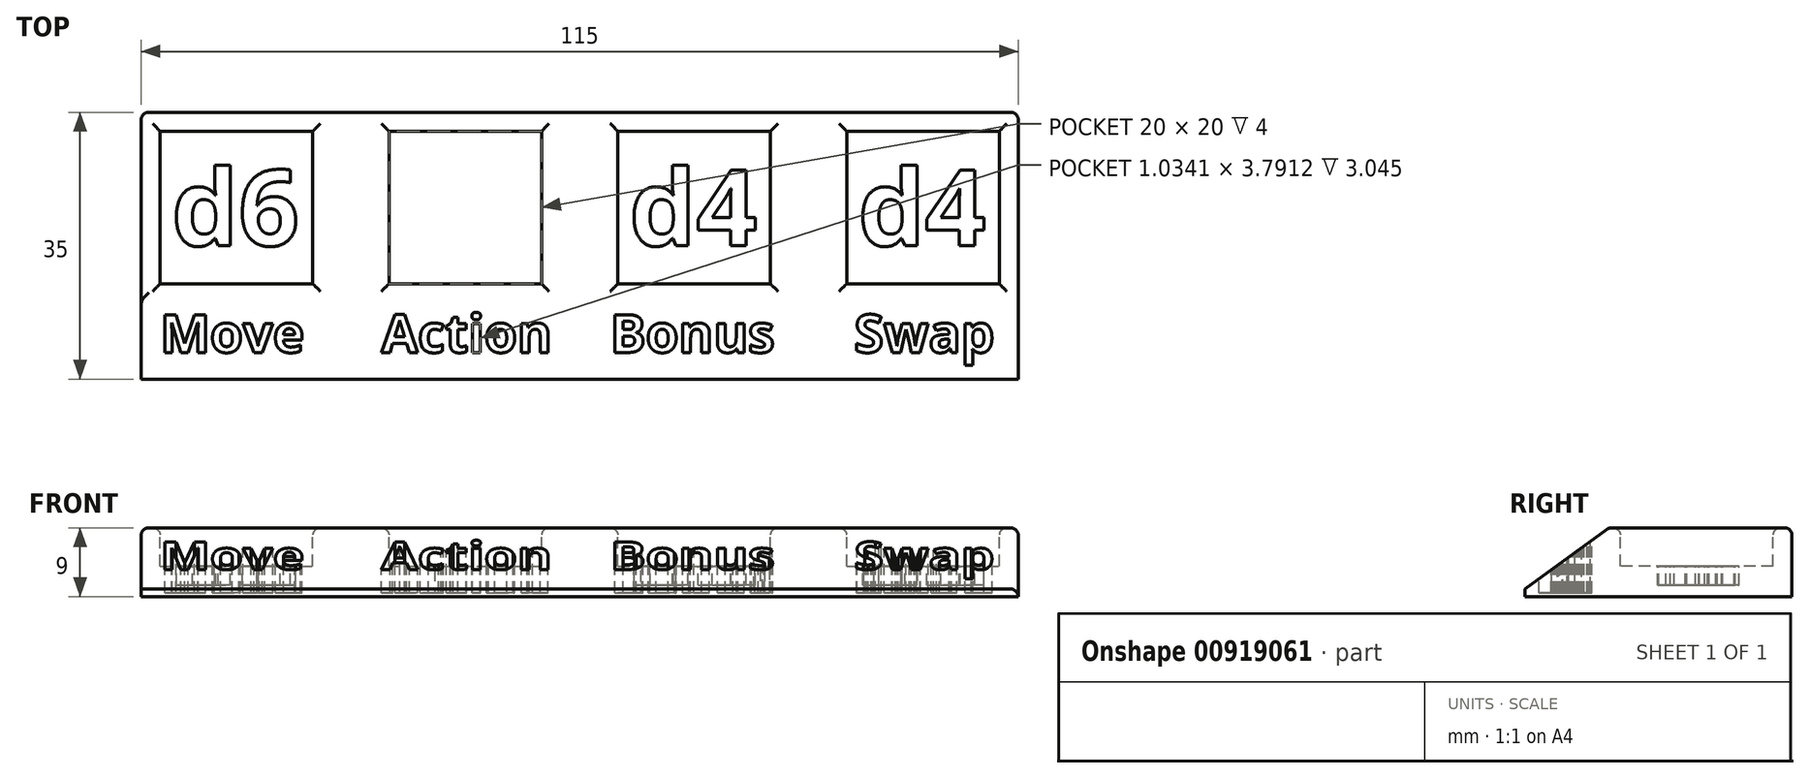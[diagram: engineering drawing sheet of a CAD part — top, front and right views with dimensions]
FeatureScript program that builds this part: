
annotation { "Feature Type Name" : "Feature", "Feature Type Description" : "" }
export const myFeature = defineFeature(function(context is Context, id is Id, definition is map)
    precondition{}
    {
        {
            var Q0;
            Q0=qCreatedBy(makeId("Top.planeOp"),FACE);
            var sketch = newSketch(context, id + "F0", { "sketchPlane" : qUnion([Q0])});
            skLineSegment(sketch, "E0.bottom", {"start": v(0, 0) * mm, "end": v(115, 0) * mm});
            skLineSegment(sketch, "E0.top", {"start": v(0, 35) * mm, "end": v(115, 35) * mm});
            skLineSegment(sketch, "E0.left", {"start": v(0, 0) * mm, "end": v(0, 35) * mm});
            skLineSegment(sketch, "E0.right", {"start": v(115, 0) * mm, "end": v(115, 35) * mm});
            skLineSegment(sketch, "E1", {"start": v(0, 32.5) * mm, "end": v(115, 32.5) * mm, "construction": true});
            skLineSegment(sketch, "E2", {"start": v(0, 12.5) * mm, "end": v(115, 12.5) * mm, "construction": true});
            skLineSegment(sketch, "E3.bottom", {"start": v(2.5, 32.5) * mm, "end": v(22.5, 32.5) * mm});
            skLineSegment(sketch, "E3.top", {"start": v(2.5, 12.5) * mm, "end": v(22.5, 12.5) * mm});
            skLineSegment(sketch, "E3.left", {"start": v(2.5, 32.5) * mm, "end": v(2.5, 12.5) * mm});
            skLineSegment(sketch, "E3.right", {"start": v(22.5, 32.5) * mm, "end": v(22.5, 12.5) * mm});
            skLineSegment(sketch, "E4.bottom", {"start": v(32.5, 32.5) * mm, "end": v(52.5, 32.5) * mm});
            skLineSegment(sketch, "E4.top", {"start": v(32.5, 12.5) * mm, "end": v(52.5, 12.5) * mm});
            skLineSegment(sketch, "E4.left", {"start": v(32.5, 32.5) * mm, "end": v(32.5, 12.5) * mm});
            skLineSegment(sketch, "E4.right", {"start": v(52.5, 32.5) * mm, "end": v(52.5, 12.5) * mm});
            skLineSegment(sketch, "E5.bottom", {"start": v(62.5, 32.5) * mm, "end": v(82.5, 32.5) * mm});
            skLineSegment(sketch, "E5.top", {"start": v(62.5, 12.5) * mm, "end": v(82.5, 12.5) * mm});
            skLineSegment(sketch, "E5.left", {"start": v(62.5, 32.5) * mm, "end": v(62.5, 12.5) * mm});
            skLineSegment(sketch, "E5.right", {"start": v(82.5, 32.5) * mm, "end": v(82.5, 12.5) * mm});
            skLineSegment(sketch, "E6.bottom", {"start": v(92.5, 32.5) * mm, "end": v(112.5, 32.5) * mm});
            skLineSegment(sketch, "E6.top", {"start": v(92.5, 12.5) * mm, "end": v(112.5, 12.5) * mm});
            skLineSegment(sketch, "E6.left", {"start": v(92.5, 32.5) * mm, "end": v(92.5, 12.5) * mm});
            skLineSegment(sketch, "E6.right", {"start": v(112.5, 32.5) * mm, "end": v(112.5, 12.5) * mm});
            skLineSegment(sketch, "E7", {"start": v(0, 27.5) * mm, "end": v(115, 27.5) * mm, "construction": true});
            skLineSegment(sketch, "E8", {"start": v(0, 17.5) * mm, "end": v(115, 17.5) * mm, "construction": true});
            skText(sketch, "E9", { "text": "d6", "fontName": "OpenSans-Bold.ttf"});
            skText(sketch, "E10", { "text": "d4", "fontName": "OpenSans-Bold.ttf"});
            skText(sketch, "E11", { "text": "d4", "fontName": "OpenSans-Bold.ttf"});
            skLineSegment(sketch, "E12", {"start": v(0, 3.5) * mm, "end": v(115, 3.5) * mm, "construction": true});
            skLineSegment(sketch, "E13", {"start": v(0, 8.5) * mm, "end": v(115, 8.5) * mm, "construction": true});
            skText(sketch, "E14", { "text": "Move", "fontName": "OpenSans-Bold.ttf"});
            skText(sketch, "E15", { "text": "Action", "fontName": "OpenSans-Bold.ttf"});
            skText(sketch, "E16", { "text": "Bonus", "fontName": "OpenSans-Bold.ttf"});
            skText(sketch, "E17", { "text": "Swap", "fontName": "OpenSans-Bold.ttf"});
            const initialGuessF0  = {"E9": [0.004, 0.0175, 1, 0, 0.01], "E10": [0.064, 0.0175, 1, 0, 0.01], "E11": [0.094, 0.0175, 1, 0, 0.01], "E14": [0.0025, 0.0035, 1, 0, 0.005], "E15": [0.0315, 0.0035, 1, 0, 0.005], "E16": [0.0615, 0.0035, 1, 0, 0.005], "E17": [0.0935, 0.0035, 1, 0, 0.005]};
            skSetInitialGuess(sketch, initialGuessF0);
            skSolve(sketch);
        }
        {
            var Q0;
            Q0=makeQuery(id+"F0.imprint","IMPRINT",FACE,{"disambiguationData":[TD([[makeQuery(id+"F0.imprint","IMPRINT",EDGE,{"derivedFrom":sQuery(id+"F0.wireOp",EDGE,"E0.bottom")}),1.0]])]});
            var Q1;
            Q1=makeQuery(id+"F0.imprint","IMPRINT",FACE,{"disambiguationData":[TD([[makeQuery(id+"F0.imprint","IMPRINT",EDGE,{"derivedFrom":sQuery(id+"F0.wireOp",EDGE,"E11.sketch_text.stroke-0")}),-1.0]])]});
            var Q2;
            Q2=makeQuery(id+"F0.imprint","IMPRINT",FACE,{"disambiguationData":[TD([[makeQuery(id+"F0.imprint","IMPRINT",EDGE,{"derivedFrom":sQuery(id+"F0.wireOp",EDGE,"E17.sketch_text.stroke-54")}),-1.0]])]});
            var Q3;
            Q3=makeQuery(id+"F0.imprint","IMPRINT",FACE,{"disambiguationData":[TD([[makeQuery(id+"F0.imprint","IMPRINT",EDGE,{"derivedFrom":sQuery(id+"F0.wireOp",EDGE,"E16.sketch_text.stroke-60")}),-1.0]])]});
            var Q4;
            Q4=makeQuery(id+"F0.imprint","IMPRINT",FACE,{"disambiguationData":[TD([[makeQuery(id+"F0.imprint","IMPRINT",EDGE,{"derivedFrom":sQuery(id+"F0.wireOp",EDGE,"E5.bottom")}),-1.0]])]});
            var Q5;
            Q5=makeQuery(id+"F0.imprint","IMPRINT",FACE,{"disambiguationData":[TD([[makeQuery(id+"F0.imprint","IMPRINT",EDGE,{"derivedFrom":sQuery(id+"F0.wireOp",EDGE,"E4.bottom")}),-1.0]])]});
            var Q6;
            Q6=makeQuery(id+"F0.imprint","IMPRINT",FACE,{"disambiguationData":[TD([[makeQuery(id+"F0.imprint","IMPRINT",EDGE,{"derivedFrom":sQuery(id+"F0.wireOp",EDGE,"E15.sketch_text.stroke-53")}),1.0]])]});
            var Q7;
            Q7=makeQuery(id+"F0.imprint","IMPRINT",FACE,{"disambiguationData":[TD([[makeQuery(id+"F0.imprint","IMPRINT",EDGE,{"derivedFrom":sQuery(id+"F0.wireOp",EDGE,"E16.sketch_text.stroke-19")}),1.0]])]});
            var Q8;
            Q8=makeQuery(id+"F0.imprint","IMPRINT",FACE,{"disambiguationData":[TD([[makeQuery(id+"F0.imprint","IMPRINT",EDGE,{"derivedFrom":sQuery(id+"F0.wireOp",EDGE,"E17.sketch_text.stroke-0")}),-1.0]])]});
            var Q9;
            Q9=makeQuery(id+"F0.imprint","IMPRINT",FACE,{"disambiguationData":[TD([[makeQuery(id+"F0.imprint","IMPRINT",EDGE,{"derivedFrom":sQuery(id+"F0.wireOp",EDGE,"E15.sketch_text.stroke-49")}),-1.0]])]});
            var Q10;
            Q10=makeQuery(id+"F0.imprint","IMPRINT",FACE,{"disambiguationData":[TD([[makeQuery(id+"F0.imprint","IMPRINT",EDGE,{"derivedFrom":sQuery(id+"F0.wireOp",EDGE,"E14.sketch_text.stroke-37")}),-1.0]])]});
            var Q11;
            Q11=makeQuery(id+"F0.imprint","IMPRINT",FACE,{"disambiguationData":[TD([[makeQuery(id+"F0.imprint","IMPRINT",EDGE,{"derivedFrom":sQuery(id+"F0.wireOp",EDGE,"E15.sketch_text.stroke-8")}),1.0]])]});
            var Q12;
            Q12=makeQuery(id+"F0.imprint","IMPRINT",FACE,{"disambiguationData":[TD([[makeQuery(id+"F0.imprint","IMPRINT",EDGE,{"derivedFrom":sQuery(id+"F0.wireOp",EDGE,"E10.sketch_text.stroke-14")}),1.0]])]});
            var Q13;
            Q13=makeQuery(id+"F0.imprint","IMPRINT",FACE,{"disambiguationData":[TD([[makeQuery(id+"F0.imprint","IMPRINT",EDGE,{"derivedFrom":sQuery(id+"F0.wireOp",EDGE,"E9.sketch_text.stroke-0")}),-1.0]])]});
            var Q14;
            Q14=makeQuery(id+"F0.imprint","IMPRINT",FACE,{"disambiguationData":[TD([[makeQuery(id+"F0.imprint","IMPRINT",EDGE,{"derivedFrom":sQuery(id+"F0.wireOp",EDGE,"E17.sketch_text.stroke-94")}),1.0]])]});
            var Q15;
            Q15=makeQuery(id+"F0.imprint","IMPRINT",FACE,{"disambiguationData":[TD([[makeQuery(id+"F0.imprint","IMPRINT",EDGE,{"derivedFrom":sQuery(id+"F0.wireOp",EDGE,"E16.sketch_text.stroke-12")}),1.0]])]});
            var Q16;
            Q16=makeQuery(id+"F0.imprint","IMPRINT",FACE,{"disambiguationData":[TD([[makeQuery(id+"F0.imprint","IMPRINT",EDGE,{"derivedFrom":sQuery(id+"F0.wireOp",EDGE,"E9.sketch_text.stroke-23")}),-1.0]])]});
            var Q17;
            Q17=makeQuery(id+"F0.imprint","IMPRINT",FACE,{"disambiguationData":[TD([[makeQuery(id+"F0.imprint","IMPRINT",EDGE,{"derivedFrom":sQuery(id+"F0.wireOp",EDGE,"E11.sketch_text.stroke-34")}),1.0]])]});
            var Q18;
            Q18=makeQuery(id+"F0.imprint","IMPRINT",FACE,{"disambiguationData":[TD([[makeQuery(id+"F0.imprint","IMPRINT",EDGE,{"derivedFrom":sQuery(id+"F0.wireOp",EDGE,"E14.sketch_text.stroke-19")}),-1.0]])]});
            var Q19;
            Q19=makeQuery(id+"F0.imprint","IMPRINT",FACE,{"disambiguationData":[TD([[makeQuery(id+"F0.imprint","IMPRINT",EDGE,{"derivedFrom":sQuery(id+"F0.wireOp",EDGE,"E15.sketch_text.stroke-53")}),-1.0]])]});
            var Q20;
            Q20=makeQuery(id+"F0.imprint","IMPRINT",FACE,{"disambiguationData":[TD([[makeQuery(id+"F0.imprint","IMPRINT",EDGE,{"derivedFrom":sQuery(id+"F0.wireOp",EDGE,"E14.sketch_text.stroke-47")}),-1.0]])]});
            var Q21;
            Q21=makeQuery(id+"F0.imprint","IMPRINT",FACE,{"disambiguationData":[TD([[makeQuery(id+"F0.imprint","IMPRINT",EDGE,{"derivedFrom":sQuery(id+"F0.wireOp",EDGE,"E17.sketch_text.stroke-72")}),1.0]])]});
            var Q22;
            Q22=makeQuery(id+"F0.imprint","IMPRINT",FACE,{"disambiguationData":[TD([[makeQuery(id+"F0.imprint","IMPRINT",EDGE,{"derivedFrom":sQuery(id+"F0.wireOp",EDGE,"E17.sketch_text.stroke-79")}),-1.0]])]});
            var Q23;
            Q23=makeQuery(id+"F0.imprint","IMPRINT",FACE,{"disambiguationData":[TD([[makeQuery(id+"F0.imprint","IMPRINT",EDGE,{"derivedFrom":sQuery(id+"F0.wireOp",EDGE,"E10.sketch_text.stroke-0")}),-1.0]])]});
            var Q24;
            Q24=makeQuery(id+"F0.imprint","IMPRINT",FACE,{"disambiguationData":[TD([[makeQuery(id+"F0.imprint","IMPRINT",EDGE,{"derivedFrom":sQuery(id+"F0.wireOp",EDGE,"E9.sketch_text.stroke-40")}),1.0]])]});
            var Q25;
            Q25=makeQuery(id+"F0.imprint","IMPRINT",FACE,{"disambiguationData":[TD([[makeQuery(id+"F0.imprint","IMPRINT",EDGE,{"derivedFrom":sQuery(id+"F0.wireOp",EDGE,"E3.bottom")}),-1.0]])]});
            var Q26;
            Q26=makeQuery(id+"F0.imprint","IMPRINT",FACE,{"disambiguationData":[TD([[makeQuery(id+"F0.imprint","IMPRINT",EDGE,{"derivedFrom":sQuery(id+"F0.wireOp",EDGE,"E15.sketch_text.stroke-71")}),-1.0]])]});
            var Q27;
            Q27=makeQuery(id+"F0.imprint","IMPRINT",FACE,{"disambiguationData":[TD([[makeQuery(id+"F0.imprint","IMPRINT",EDGE,{"derivedFrom":sQuery(id+"F0.wireOp",EDGE,"E14.sketch_text.stroke-0")}),-1.0]])]});
            var Q28;
            Q28=makeQuery(id+"F0.imprint","IMPRINT",FACE,{"disambiguationData":[TD([[makeQuery(id+"F0.imprint","IMPRINT",EDGE,{"derivedFrom":sQuery(id+"F0.wireOp",EDGE,"E6.bottom")}),-1.0]])]});
            var Q29;
            Q29=makeQuery(id+"F0.imprint","IMPRINT",FACE,{"disambiguationData":[TD([[makeQuery(id+"F0.imprint","IMPRINT",EDGE,{"derivedFrom":sQuery(id+"F0.wireOp",EDGE,"E10.sketch_text.stroke-23")}),-1.0]])]});
            var Q30;
            Q30=makeQuery(id+"F0.imprint","IMPRINT",FACE,{"disambiguationData":[TD([[makeQuery(id+"F0.imprint","IMPRINT",EDGE,{"derivedFrom":sQuery(id+"F0.wireOp",EDGE,"E17.sketch_text.stroke-28")}),-1.0]])]});
            var Q31;
            Q31=makeQuery(id+"F0.imprint","IMPRINT",FACE,{"disambiguationData":[TD([[makeQuery(id+"F0.imprint","IMPRINT",EDGE,{"derivedFrom":sQuery(id+"F0.wireOp",EDGE,"E16.sketch_text.stroke-43")}),-1.0]])]});
            var Q32;
            Q32=makeQuery(id+"F0.imprint","IMPRINT",FACE,{"disambiguationData":[TD([[makeQuery(id+"F0.imprint","IMPRINT",EDGE,{"derivedFrom":sQuery(id+"F0.wireOp",EDGE,"E16.sketch_text.stroke-0")}),-1.0]])]});
            var Q33;
            Q33=makeQuery(id+"F0.imprint","IMPRINT",FACE,{"disambiguationData":[TD([[makeQuery(id+"F0.imprint","IMPRINT",EDGE,{"derivedFrom":sQuery(id+"F0.wireOp",EDGE,"E15.sketch_text.stroke-12")}),-1.0]])]});
            var Q34;
            Q34=makeQuery(id+"F0.imprint","IMPRINT",FACE,{"disambiguationData":[TD([[makeQuery(id+"F0.imprint","IMPRINT",EDGE,{"derivedFrom":sQuery(id+"F0.wireOp",EDGE,"E16.sketch_text.stroke-25")}),-1.0]])]});
            var Q35;
            Q35=makeQuery(id+"F0.imprint","IMPRINT",FACE,{"disambiguationData":[TD([[makeQuery(id+"F0.imprint","IMPRINT",EDGE,{"derivedFrom":sQuery(id+"F0.wireOp",EDGE,"E16.sketch_text.stroke-77")}),-1.0]])]});
            var Q36;
            Q36=makeQuery(id+"F0.imprint","IMPRINT",FACE,{"disambiguationData":[TD([[makeQuery(id+"F0.imprint","IMPRINT",EDGE,{"derivedFrom":sQuery(id+"F0.wireOp",EDGE,"E15.sketch_text.stroke-0")}),-1.0]])]});
            var Q37;
            Q37=makeQuery(id+"F0.imprint","IMPRINT",FACE,{"disambiguationData":[TD([[makeQuery(id+"F0.imprint","IMPRINT",EDGE,{"derivedFrom":sQuery(id+"F0.wireOp",EDGE,"E14.sketch_text.stroke-19")}),1.0]])]});
            var Q38;
            Q38=makeQuery(id+"F0.imprint","IMPRINT",FACE,{"disambiguationData":[TD([[makeQuery(id+"F0.imprint","IMPRINT",EDGE,{"derivedFrom":sQuery(id+"F0.wireOp",EDGE,"E9.sketch_text.stroke-14")}),1.0]])]});
            var Q39;
            Q39=makeQuery(id+"F0.imprint","IMPRINT",FACE,{"disambiguationData":[TD([[makeQuery(id+"F0.imprint","IMPRINT",EDGE,{"derivedFrom":sQuery(id+"F0.wireOp",EDGE,"E11.sketch_text.stroke-14")}),1.0]])]});
            var Q40;
            Q40=makeQuery(id+"F0.imprint","IMPRINT",FACE,{"disambiguationData":[TD([[makeQuery(id+"F0.imprint","IMPRINT",EDGE,{"derivedFrom":sQuery(id+"F0.wireOp",EDGE,"E10.sketch_text.stroke-34")}),1.0]])]});
            var Q41;
            Q41=makeQuery(id+"F0.imprint","IMPRINT",FACE,{"disambiguationData":[TD([[makeQuery(id+"F0.imprint","IMPRINT",EDGE,{"derivedFrom":sQuery(id+"F0.wireOp",EDGE,"E11.sketch_text.stroke-23")}),-1.0]])]});
            var Q42;
            Q42=makeQuery(id+"F0.imprint","IMPRINT",FACE,{"disambiguationData":[TD([[makeQuery(id+"F0.imprint","IMPRINT",EDGE,{"derivedFrom":sQuery(id+"F0.wireOp",EDGE,"E16.sketch_text.stroke-25")}),1.0]])]});
            var Q43;
            Q43=makeQuery(id+"F0.imprint","IMPRINT",FACE,{"disambiguationData":[TD([[makeQuery(id+"F0.imprint","IMPRINT",EDGE,{"derivedFrom":sQuery(id+"F0.wireOp",EDGE,"E14.sketch_text.stroke-47")}),1.0]])]});
            var Q44;
            Q44=makeQuery(id+"F0.imprint","IMPRINT",FACE,{"disambiguationData":[TD([[makeQuery(id+"F0.imprint","IMPRINT",EDGE,{"derivedFrom":sQuery(id+"F0.wireOp",EDGE,"E15.sketch_text.stroke-26")}),-1.0]])]});
            var Q45;
            Q45=makeQuery(id+"F0.imprint","IMPRINT",FACE,{"disambiguationData":[TD([[makeQuery(id+"F0.imprint","IMPRINT",EDGE,{"derivedFrom":sQuery(id+"F0.wireOp",EDGE,"E15.sketch_text.stroke-44")}),-1.0]])]});
            extrude(context, id + "F1", {"entities" : qUnion([Q0, Q1, Q2, Q3, Q4, Q5, Q6, Q7, Q8, Q9, Q10, Q11, Q12, Q13, Q14, Q15, Q16, Q17, Q18, Q19, Q20, Q21, Q22, Q23, Q24, Q25, Q26, Q27, Q28, Q29, Q30, Q31, Q32, Q33, Q34, Q35, Q36, Q37, Q38, Q39, Q40, Q41, Q42, Q43, Q44, Q45]), "oppositeDirection" : true, "depth" : 9 * mm, "offsetDistance" : 25 * mm});
        }
        {
            var Q0;
            Q0=makeQuery(id+"F0.imprint","IMPRINT",FACE,{"disambiguationData":[TD([[makeQuery(id+"F0.imprint","IMPRINT",EDGE,{"derivedFrom":sQuery(id+"F0.wireOp",EDGE,"E3.bottom")}),-1.0]])]});
            var Q1;
            Q1=makeQuery(id+"F0.imprint","IMPRINT",FACE,{"disambiguationData":[TD([[makeQuery(id+"F0.imprint","IMPRINT",EDGE,{"derivedFrom":sQuery(id+"F0.wireOp",EDGE,"E4.bottom")}),-1.0]])]});
            var Q2;
            Q2=makeQuery(id+"F0.imprint","IMPRINT",FACE,{"disambiguationData":[TD([[makeQuery(id+"F0.imprint","IMPRINT",EDGE,{"derivedFrom":sQuery(id+"F0.wireOp",EDGE,"E5.bottom")}),-1.0]])]});
            var Q3;
            Q3=makeQuery(id+"F0.imprint","IMPRINT",FACE,{"disambiguationData":[TD([[makeQuery(id+"F0.imprint","IMPRINT",EDGE,{"derivedFrom":sQuery(id+"F0.wireOp",EDGE,"E6.bottom")}),-1.0]])]});
            var Q4;
            Q4=makeQuery(id+"F0.imprint","IMPRINT",FACE,{"disambiguationData":[TD([[makeQuery(id+"F0.imprint","IMPRINT",EDGE,{"derivedFrom":sQuery(id+"F0.wireOp",EDGE,"E10.sketch_text.stroke-14")}),1.0]])]});
            var Q5;
            Q5=makeQuery(id+"F0.imprint","IMPRINT",FACE,{"disambiguationData":[TD([[makeQuery(id+"F0.imprint","IMPRINT",EDGE,{"derivedFrom":sQuery(id+"F0.wireOp",EDGE,"E9.sketch_text.stroke-40")}),1.0]])]});
            var Q6;
            Q6=makeQuery(id+"F0.imprint","IMPRINT",FACE,{"disambiguationData":[TD([[makeQuery(id+"F0.imprint","IMPRINT",EDGE,{"derivedFrom":sQuery(id+"F0.wireOp",EDGE,"E9.sketch_text.stroke-14")}),1.0]])]});
            var Q7;
            Q7=makeQuery(id+"F0.imprint","IMPRINT",FACE,{"disambiguationData":[TD([[makeQuery(id+"F0.imprint","IMPRINT",EDGE,{"derivedFrom":sQuery(id+"F0.wireOp",EDGE,"E11.sketch_text.stroke-14")}),1.0]])]});
            var Q8;
            Q8=makeQuery(id+"F0.imprint","IMPRINT",FACE,{"disambiguationData":[TD([[makeQuery(id+"F0.imprint","IMPRINT",EDGE,{"derivedFrom":sQuery(id+"F0.wireOp",EDGE,"E10.sketch_text.stroke-34")}),1.0]])]});
            var Q9;
            Q9=makeQuery(id+"F0.imprint","IMPRINT",FACE,{"disambiguationData":[TD([[makeQuery(id+"F0.imprint","IMPRINT",EDGE,{"derivedFrom":sQuery(id+"F0.wireOp",EDGE,"E11.sketch_text.stroke-34")}),1.0]])]});
            extrude(context, id + "F2", {"entities" : qUnion([Q0, Q1, Q2, Q3, Q4, Q5, Q6, Q7, Q8, Q9]), "operationType" : NewBodyOperationType.REMOVE, "oppositeDirection" : true, "depth" : 5 * mm, "offsetDistance" : 25 * mm});
        }
        {
            var Q0;
            Q0=makeQuery(id+"F0.imprint","IMPRINT",FACE,{"disambiguationData":[TD([[makeQuery(id+"F0.imprint","IMPRINT",EDGE,{"derivedFrom":sQuery(id+"F0.wireOp",EDGE,"E9.sketch_text.stroke-0")}),-1.0]])]});
            var Q1;
            Q1=makeQuery(id+"F0.imprint","IMPRINT",FACE,{"disambiguationData":[TD([[makeQuery(id+"F0.imprint","IMPRINT",EDGE,{"derivedFrom":sQuery(id+"F0.wireOp",EDGE,"E9.sketch_text.stroke-23")}),-1.0]])]});
            var Q2;
            Q2=makeQuery(id+"F0.imprint","IMPRINT",FACE,{"disambiguationData":[TD([[makeQuery(id+"F0.imprint","IMPRINT",EDGE,{"derivedFrom":sQuery(id+"F0.wireOp",EDGE,"E10.sketch_text.stroke-0")}),-1.0]])]});
            var Q3;
            Q3=makeQuery(id+"F0.imprint","IMPRINT",FACE,{"disambiguationData":[TD([[makeQuery(id+"F0.imprint","IMPRINT",EDGE,{"derivedFrom":sQuery(id+"F0.wireOp",EDGE,"E10.sketch_text.stroke-23")}),-1.0]])]});
            var Q4;
            Q4=makeQuery(id+"F0.imprint","IMPRINT",FACE,{"disambiguationData":[TD([[makeQuery(id+"F0.imprint","IMPRINT",EDGE,{"derivedFrom":sQuery(id+"F0.wireOp",EDGE,"E11.sketch_text.stroke-0")}),-1.0]])]});
            var Q5;
            Q5=makeQuery(id+"F0.imprint","IMPRINT",FACE,{"disambiguationData":[TD([[makeQuery(id+"F0.imprint","IMPRINT",EDGE,{"derivedFrom":sQuery(id+"F0.wireOp",EDGE,"E11.sketch_text.stroke-23")}),-1.0]])]});
            extrude(context, id + "F3", {"entities" : qUnion([Q0, Q1, Q2, Q3, Q4, Q5]), "operationType" : NewBodyOperationType.REMOVE, "oppositeDirection" : true, "depth" : 7.5 * mm, "offsetDistance" : 25 * mm});
        }
        {
            var Q0;
            Q0=makeQuery(id+"F0.imprint","IMPRINT",FACE,{"disambiguationData":[TD([[makeQuery(id+"F0.imprint","IMPRINT",EDGE,{"derivedFrom":sQuery(id+"F0.wireOp",EDGE,"E14.sketch_text.stroke-47")}),-1.0]])]});
            var Q1;
            Q1=makeQuery(id+"F0.imprint","IMPRINT",FACE,{"disambiguationData":[TD([[makeQuery(id+"F0.imprint","IMPRINT",EDGE,{"derivedFrom":sQuery(id+"F0.wireOp",EDGE,"E14.sketch_text.stroke-37")}),-1.0]])]});
            var Q2;
            Q2=makeQuery(id+"F0.imprint","IMPRINT",FACE,{"disambiguationData":[TD([[makeQuery(id+"F0.imprint","IMPRINT",EDGE,{"derivedFrom":sQuery(id+"F0.wireOp",EDGE,"E14.sketch_text.stroke-19")}),-1.0]])]});
            var Q3;
            Q3=makeQuery(id+"F0.imprint","IMPRINT",FACE,{"disambiguationData":[TD([[makeQuery(id+"F0.imprint","IMPRINT",EDGE,{"derivedFrom":sQuery(id+"F0.wireOp",EDGE,"E14.sketch_text.stroke-0")}),-1.0]])]});
            var Q4;
            Q4=makeQuery(id+"F0.imprint","IMPRINT",FACE,{"disambiguationData":[TD([[makeQuery(id+"F0.imprint","IMPRINT",EDGE,{"derivedFrom":sQuery(id+"F0.wireOp",EDGE,"E15.sketch_text.stroke-0")}),-1.0]])]});
            var Q5;
            Q5=makeQuery(id+"F0.imprint","IMPRINT",FACE,{"disambiguationData":[TD([[makeQuery(id+"F0.imprint","IMPRINT",EDGE,{"derivedFrom":sQuery(id+"F0.wireOp",EDGE,"E15.sketch_text.stroke-12")}),-1.0]])]});
            var Q6;
            Q6=makeQuery(id+"F0.imprint","IMPRINT",FACE,{"disambiguationData":[TD([[makeQuery(id+"F0.imprint","IMPRINT",EDGE,{"derivedFrom":sQuery(id+"F0.wireOp",EDGE,"E15.sketch_text.stroke-26")}),-1.0]])]});
            var Q7;
            Q7=makeQuery(id+"F0.imprint","IMPRINT",FACE,{"disambiguationData":[TD([[makeQuery(id+"F0.imprint","IMPRINT",EDGE,{"derivedFrom":sQuery(id+"F0.wireOp",EDGE,"E15.sketch_text.stroke-49")}),-1.0]])]});
            var Q8;
            Q8=makeQuery(id+"F0.imprint","IMPRINT",FACE,{"disambiguationData":[TD([[makeQuery(id+"F0.imprint","IMPRINT",EDGE,{"derivedFrom":sQuery(id+"F0.wireOp",EDGE,"E15.sketch_text.stroke-53")}),-1.0]])]});
            var Q9;
            Q9=makeQuery(id+"F0.imprint","IMPRINT",FACE,{"disambiguationData":[TD([[makeQuery(id+"F0.imprint","IMPRINT",EDGE,{"derivedFrom":sQuery(id+"F0.wireOp",EDGE,"E15.sketch_text.stroke-71")}),-1.0]])]});
            var Q10;
            Q10=makeQuery(id+"F0.imprint","IMPRINT",FACE,{"disambiguationData":[TD([[makeQuery(id+"F0.imprint","IMPRINT",EDGE,{"derivedFrom":sQuery(id+"F0.wireOp",EDGE,"E16.sketch_text.stroke-0")}),-1.0]])]});
            var Q11;
            Q11=makeQuery(id+"F0.imprint","IMPRINT",FACE,{"disambiguationData":[TD([[makeQuery(id+"F0.imprint","IMPRINT",EDGE,{"derivedFrom":sQuery(id+"F0.wireOp",EDGE,"E16.sketch_text.stroke-25")}),-1.0]])]});
            var Q12;
            Q12=makeQuery(id+"F0.imprint","IMPRINT",FACE,{"disambiguationData":[TD([[makeQuery(id+"F0.imprint","IMPRINT",EDGE,{"derivedFrom":sQuery(id+"F0.wireOp",EDGE,"E16.sketch_text.stroke-43")}),-1.0]])]});
            var Q13;
            Q13=makeQuery(id+"F0.imprint","IMPRINT",FACE,{"disambiguationData":[TD([[makeQuery(id+"F0.imprint","IMPRINT",EDGE,{"derivedFrom":sQuery(id+"F0.wireOp",EDGE,"E16.sketch_text.stroke-60")}),-1.0]])]});
            var Q14;
            Q14=makeQuery(id+"F0.imprint","IMPRINT",FACE,{"disambiguationData":[TD([[makeQuery(id+"F0.imprint","IMPRINT",EDGE,{"derivedFrom":sQuery(id+"F0.wireOp",EDGE,"E16.sketch_text.stroke-77")}),-1.0]])]});
            var Q15;
            Q15=makeQuery(id+"F0.imprint","IMPRINT",FACE,{"disambiguationData":[TD([[makeQuery(id+"F0.imprint","IMPRINT",EDGE,{"derivedFrom":sQuery(id+"F0.wireOp",EDGE,"E17.sketch_text.stroke-0")}),-1.0]])]});
            var Q16;
            Q16=makeQuery(id+"F0.imprint","IMPRINT",FACE,{"disambiguationData":[TD([[makeQuery(id+"F0.imprint","IMPRINT",EDGE,{"derivedFrom":sQuery(id+"F0.wireOp",EDGE,"E17.sketch_text.stroke-54")}),-1.0]])]});
            var Q17;
            Q17=makeQuery(id+"F0.imprint","IMPRINT",FACE,{"disambiguationData":[TD([[makeQuery(id+"F0.imprint","IMPRINT",EDGE,{"derivedFrom":sQuery(id+"F0.wireOp",EDGE,"E17.sketch_text.stroke-79")}),-1.0]])]});
            var Q18;
            Q18=makeQuery(id+"F0.imprint","IMPRINT",FACE,{"disambiguationData":[TD([[makeQuery(id+"F0.imprint","IMPRINT",EDGE,{"derivedFrom":sQuery(id+"F0.wireOp",EDGE,"E17.sketch_text.stroke-28")}),-1.0]])]});
            var Q19;
            Q19=makeQuery(id+"F0.imprint","IMPRINT",FACE,{"disambiguationData":[TD([[makeQuery(id+"F0.imprint","IMPRINT",EDGE,{"derivedFrom":sQuery(id+"F0.wireOp",EDGE,"E15.sketch_text.stroke-44")}),-1.0]])]});
            extrude(context, id + "F4", {"entities" : qUnion([Q0, Q1, Q2, Q3, Q4, Q5, Q6, Q7, Q8, Q9, Q10, Q11, Q12, Q13, Q14, Q15, Q16, Q17, Q18, Q19]), "operationType" : NewBodyOperationType.REMOVE, "oppositeDirection" : true, "depth" : 8.5 * mm, "offsetDistance" : 25 * mm});
        }
        {
            var Q0;
            Q0=qCreatedBy(makeId("Right.planeOp"),FACE);
            var sketch = newSketch(context, id + "F5", { "sketchPlane" : qUnion([Q0])});
            skLineSegment(sketch, "E18", {"start": v(11, 0) * mm, "end": v(11, -8) * mm, "construction": true});
            skLineSegment(sketch, "E19", {"start": v(11, -8) * mm, "end": v(0, -8) * mm, "construction": true});
            skLineSegment(sketch, "E20", {"start": v(11, 0) * mm, "end": v(0, -8) * mm});
            skLineSegment(sketch, "E21", {"start": v(11, 0) * mm, "end": v(0, 0) * mm});
            skLineSegment(sketch, "E22", {"start": v(0, 0) * mm, "end": v(0, -8) * mm});
            skSolve(sketch);
        }
        {
            var Q0;
            Q0=makeQuery(id+"F5.imprint","IMPRINT",FACE,{"disambiguationData":[TD([[makeQuery(id+"F5.imprint","IMPRINT",EDGE,{"derivedFrom":sQuery(id+"F5.wireOp",EDGE,"E20")}),-1.0]])]});
            extrude(context, id + "F6", {"entities" : qUnion([Q0]), "operationType" : NewBodyOperationType.REMOVE, "depth" : 120 * mm, "offsetDistance" : 25 * mm});
        }
        {
            var Q0;
            Q0=makeQuery(id+"F1.opExtrude","CAP_EDGE",EDGE,{"disambiguationData":[OSD([sQuery(id+"F0.wireOp",EDGE,"E0.top")])],"isStart":true});
            var Q1;
            Q1=makeQuery(id+"F1.opExtrude","CAP_EDGE",EDGE,{"disambiguationData":[OSD([sQuery(id+"F0.wireOp",EDGE,"E0.right")])],"isStart":true});
            var Q2;
            Q2=makeQuery(id+"F6.boolean.opBoolean","INTERSECT",EDGE,{"derivedFrom":[makeQuery(id+"F1.opExtrude","SWEPT_FACE",FACE,{"disambiguationData":[OSD([sQuery(id+"F0.wireOp",EDGE,"E0.right")])]}),makeQuery(id+"F6.opExtrude","SWEPT_FACE",FACE,{"disambiguationData":[OSD([sQuery(id+"F5.wireOp",EDGE,"E20")])]})]});
            var Q3;
            Q3=makeQuery(id+"F6.boolean.opBoolean","COPY",EDGE,{"derivedFrom":makeQuery(id+"F6.opExtrude","SWEPT_EDGE",EDGE,{"disambiguationData":[OSD([sQuery(id+"F5.wireOp",EDGE,"E20"),sQuery(id+"F5.wireOp",EDGE,"E21")])]})});
            var Q4;
            Q4=makeQuery(id+"F1.opExtrude","CAP_EDGE",EDGE,{"disambiguationData":[OSD([sQuery(id+"F0.wireOp",EDGE,"E0.left")])],"isStart":true});
            var Q5;
            Q5=makeQuery(id+"F6.boolean.opBoolean","COPY",EDGE,{"derivedFrom":makeQuery(id+"F6.opExtrude","SWEPT_EDGE",EDGE,{"disambiguationData":[OSD([sQuery(id+"F5.wireOp",EDGE,"E20"),sQuery(id+"F5.wireOp",EDGE,"E22")])]})});
            var Q6;
            Q6=makeQuery(id+"F6.boolean.opBoolean","COPY",EDGE,{"derivedFrom":makeQuery(id+"F6.opExtrude","CAP_EDGE",EDGE,{"disambiguationData":[OSD([sQuery(id+"F5.wireOp",EDGE,"E20")])],"isStart":true})});
            var Q7;
            Q7=makeQuery(id+"F1.opExtrude","SWEPT_EDGE",EDGE,{"disambiguationData":[OSD([sQuery(id+"F0.wireOp",EDGE,"E0.top"),sQuery(id+"F0.wireOp",EDGE,"E0.left")])]});
            var Q8;
            Q8=makeQuery(id+"F1.opExtrude","SWEPT_EDGE",EDGE,{"disambiguationData":[OSD([sQuery(id+"F0.wireOp",EDGE,"E0.top"),sQuery(id+"F0.wireOp",EDGE,"E0.right")])]});
            var Q9;
            Q9=makeQuery(id+"F2.boolean.opBoolean","COPY",EDGE,{"derivedFrom":makeQuery(id+"F2.opExtrude","CAP_EDGE",EDGE,{"disambiguationData":[OSD([sQuery(id+"F0.wireOp",EDGE,"E6.left")])],"isStart":true})});
            var Q10;
            Q10=makeQuery(id+"F2.boolean.opBoolean","COPY",EDGE,{"derivedFrom":makeQuery(id+"F2.opExtrude","CAP_EDGE",EDGE,{"disambiguationData":[OSD([sQuery(id+"F0.wireOp",EDGE,"E6.bottom")])],"isStart":true})});
            var Q11;
            Q11=makeQuery(id+"F2.boolean.opBoolean","COPY",EDGE,{"derivedFrom":makeQuery(id+"F2.opExtrude","CAP_EDGE",EDGE,{"disambiguationData":[OSD([sQuery(id+"F0.wireOp",EDGE,"E6.right")])],"isStart":true})});
            var Q12;
            Q12=makeQuery(id+"F2.boolean.opBoolean","COPY",EDGE,{"derivedFrom":makeQuery(id+"F2.opExtrude","CAP_EDGE",EDGE,{"disambiguationData":[OSD([sQuery(id+"F0.wireOp",EDGE,"E6.top")])],"isStart":true})});
            var Q13;
            Q13=makeQuery(id+"F2.boolean.opBoolean","COPY",EDGE,{"derivedFrom":makeQuery(id+"F2.opExtrude","CAP_EDGE",EDGE,{"disambiguationData":[OSD([sQuery(id+"F0.wireOp",EDGE,"E5.right")])],"isStart":true})});
            var Q14;
            {var subQ1=sQuery(id+"F0.wireOp",EDGE,"E0.bottom");var subQ2=makeQuery(id+"F1.opExtrude","SWEPT_FACE",FACE,{"disambiguationData":[OSD([subQ1])]});var subQ7=sQuery(id+"F0.wireOp",EDGE,"E0.right");var subQ11=sQuery(id+"F0.wireOp",EDGE,"E0.top");var subQ15=sQuery(id+"F0.wireOp",EDGE,"E0.left");Q14=makeQuery(id+"F4.boolean.opBoolean","SPLIT",FACE,{"disambiguationData":[TD([subQ2])],"derivedFrom":makeQuery(id+"F2.boolean.opBoolean","SPLIT",FACE,{"disambiguationData":[TD([subQ2])],"derivedFrom":makeQuery(id+"F1.opExtrude","CAP_FACE",FACE,{"disambiguationData":[OSD([subQ1,subQ11,subQ15,subQ7])],"isStart":true})})});}
            fillet(context, id + "F7", {"entities" : qUnion([Q0, Q1, Q2, Q3, Q4, Q5, Q6, Q7, Q8, Q9, Q10, Q11, Q12, Q13, Q14]), "radius" : 1 * mm, "tangentPropagation" : true, "allowEdgeOverflow" : false});
        }
    });
